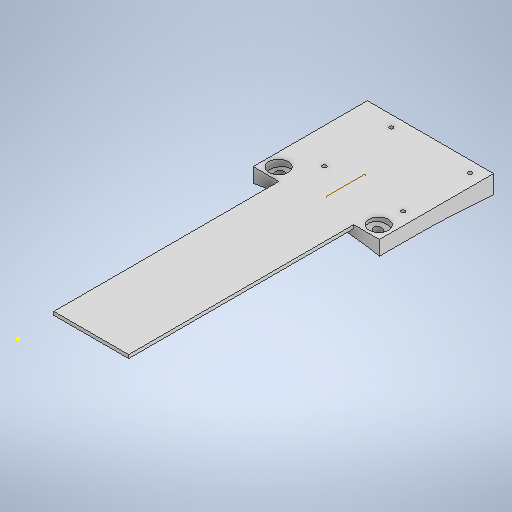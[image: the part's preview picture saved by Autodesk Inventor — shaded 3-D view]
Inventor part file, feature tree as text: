
AUTODESK INVENTOR PART (.ipt)
format: ipt  version: 2025 (Build 290162000, 162)  size: 465,920 bytes
history: native  units: in
note: dims shown in document units (in); Inventor stores cm internally (conversion verified against a paired STEP export)
features: sketch x10, extrude x7, mirror x2, other x2, revolve x1, plane x1, loft x1
ambient origin geometry x8: Origin, YZ Plane, XZ Plane, XY Plane, X Axis, Y Axis, Z Axis, Center Point
bodies: Solid1 (feature_tree)
feature tree (24):
  extrude  "Extrusion1"  Depth=1.5in
  revolve  "Revolution1"  [1 undecoded]
  extrude  "Extrusion2"  Depth=0.0563in
  plane  "Work Plane9"
  mirror  "Mirror1"
  extrude  "Extrusion3"  TaperAngle=90.0deg  [1 undecoded]
  mirror  "Mirror2"
  extrude  "Extrusion4"  TaperAngle=90.0deg  [1 undecoded]
  extrude  "Extrusion5"  Depth=0.6748in
  extrude  "Extrusion13"  TaperAngle=180.0deg  [1 undecoded]
  loft  "Loft4"
  extrude  "Extrusion14"  Depth=0.356in
  sketch  "Sketch21"  dims[d31=90.0deg d32=0.712in d33=1.0in d34=0.0in d52=2.585in d53=2.585in d54=0.36in d55=0.33in d56=0.11in d57=2.27in d58=1.93in d59=0.11in d60=0.11in d61=0.11in d62=0.2in d63=0.0in d64=0.345in d65=0.099in d66=0.099in d76=0.11in d113=0.01in d114=0.01in d115=0.01in d116=0.001in d117=0.0in d118=29.638in d119=0.0in d120=90.0deg d121=0.0in d122=90.0deg d123=0.0in d124=90.0deg d125=6.5in d126=1.08in d127=1.08in d128=0.1in d129=0.0in d95=0.5in d96=0.0344in d97=0.5in d98=0.0344in]
  sketch  "Sketch1"  dims[d2=0.25in d3=1.5in]
  sketch  "Sketch2"  dims[d4=1.0in d5=0.0in d6=0.1in]
  sketch  "Sketch3"  dims[d7=0.12in d8=0.0563in]
  sketch  "Sketch5"  dims[d9=0.2in d10=90.0deg]
  sketch  "Sketch6"  dims[d11=0.275in d12=90.0deg]
  sketch  "Sketch7"  dims[d13=0.15in d14=0.6748in]
  sketch  "Sketch8"  dims[d15=0.1in d16=180.0deg]
  sketch  "Sketch19"  dims[d17=1.0in d18=0.0in d27=-1.8228in]
  other  "Edges7"
  other  "Edges8"
  sketch  "Sketch20"  dims[d28=1.0in d29=0.0in d30=0.356in]
note: 4 required parameter values undecoded (feature->parameter linkage not recoverable at this tier; creation-order binding heuristic only, values carry confidence <= 0.55)